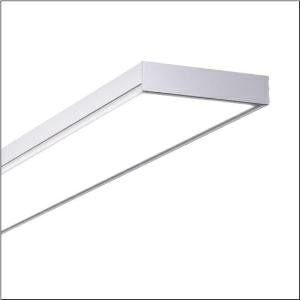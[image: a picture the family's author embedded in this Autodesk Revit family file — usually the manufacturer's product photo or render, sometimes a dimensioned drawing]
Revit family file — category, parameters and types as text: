
# Revit family: apollon_r__31_surface_51mp25wd2341e_9687
name_source: partatom
category: Lighting Fixtures
units: mm (PartAtom-declared; Revit-internal decimal feet)

## family parameters
Cut with Voids When Loaded = No
Host = Face
Light Source = No
Part Type = Normal
Room Calculation Point = No
Round Connector Dimension = Use Diameter
Shared = No

## types (1)
- Apollon® 31 Surface (1 x LED, 3600 lm, 28 W, 3000K)
    Apparent Load = 28 VA
    CIE Flux Codes = 61 87 97 97 100
    Color Rendering = 80
    Color Temperature = 3000K
    Default Elevation = 1800 mm
    Description = Apollon® 31 Surface, office luminaire, primary optical cover: micro prismatic cover, of PMMA, light emission: direct distribution, primary light characteristic: symmetric, installation type: surface-mounted, LED, rated luminous flux: 3.600lm, luminous efficacy: 128lm/W, light colour: 830, colour temperature: 3000K, control gear: ECG DALI, with terminal, 5-pole, mains connection: 220..240V, AC, 50/60Hz, rated input power: 28W, housing, of sheet steel, coil coated, metallic grey (RAL 9006), length: 1.245mm, width: 200mm, height: 44mm, protection rating (complete): IP20, insulation class (complete): insulation class II (safety insulation), certification: CE, impact resistance: IK02, permissible operating ambient temperature: -20..+40°C, standard: EN 60598-2-22, packaging unit: 1 piece
    Height = 44 mm
    Lamp = 1 x LED
    Lamp Light Flux = 3600 lm
    Lamp Power = 28 W
    Lamp count = 1
    Length = 1245 mm
    Luminous efficacy = 129 lm/W
    Manufacturer = Siteco
    ModVariant = No
    Model = 51MP25WD2341E
    Mounting Place = Ceiling
    Mounting Type = Surface mounted
    Number of Poles = 1
    OnlyDefault = Yes
    Power Factor = 1
    Product Name = Apollon® 31 Surface
    Product group = office luminaire | ceiling mounted
    ProductGroupID = 304
    Protection Class = Protection class II
    Protection Degree = IP 20
    RLX_Detail_Level = 1
    RLX_Emergency_Light_Flux = 0 lm
    RLX_Emergency_Type = 0
    RLX_Emergency_Type_DB = No
    RlxData = <blob elided: 24105 chars, md5=3d669151>
    Socket = socket
    Standby Power = 0 W
    System Light Flux = 3600 lm
    System Power = 28 W
    Type Comments = Product without accessories
    Type Image = l_1007091.jpg
    URL = http://relux.com
    VarID = ---
    Voltage = 0 V
    Weight = 0.00 kg
    Width = 200 mm  [stored 0.656168 ft]

note: [stored X ft] marks values corroborated as IEEE doubles in the binary element streams (Revit-internal decimal feet)

## geometry (parser evidence)
native form markers: Blend x4, Sweep x10
no freeform markers — native parametric forms only
